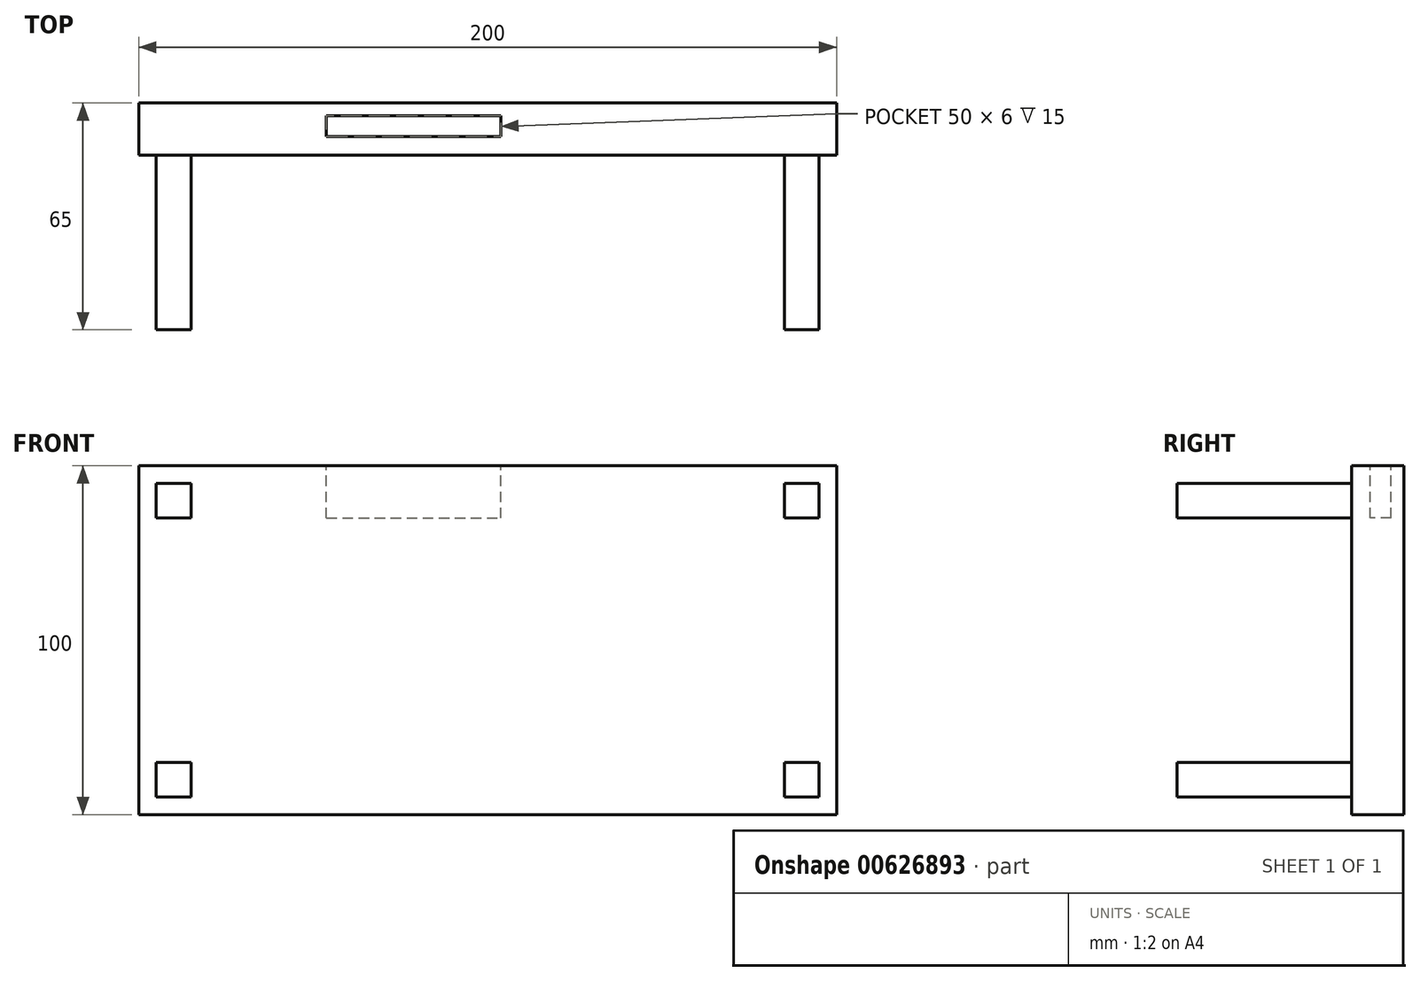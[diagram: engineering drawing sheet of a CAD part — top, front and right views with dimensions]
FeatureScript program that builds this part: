
annotation { "Feature Type Name" : "Feature", "Feature Type Description" : "" }
export const myFeature = defineFeature(function(context is Context, id is Id, definition is map)
    precondition{}
    {
        {
            var Q0;
            Q0=qCreatedBy(makeId("Front.planeOp"),FACE);
            var sketch = newSketch(context, id + "F0", { "sketchPlane" : qUnion([Q0])});
            skLineSegment(sketch, "E0.bottom", {"start": v(-53.8, 99.96) * mm, "end": v(146.2, 99.96) * mm});
            skLineSegment(sketch, "E0.top", {"start": v(-53.8, -0.04) * mm, "end": v(146.2, -0.04) * mm});
            skLineSegment(sketch, "E0.left", {"start": v(-53.8, 99.96) * mm, "end": v(-53.8, -0.04) * mm});
            skLineSegment(sketch, "E0.right", {"start": v(146.2, 99.96) * mm, "end": v(146.2, -0.04) * mm});
            skSolve(sketch);
        }
        {
            var Q0;
            Q0 = qSketchRegion(id + "F0", true);
            extrude(context, id + "F1", {"entities" : qUnion([Q0]), "depth" : 15 * mm, "offsetDistance" : 25 * mm});
        }
        {
            var Q0;
            Q0=makeQuery(id+"F1.opExtrude","CAP_FACE",FACE,{"disambiguationData":[OSD([sQuery(id+"F0.wireOp",EDGE,"E0.bottom"),sQuery(id+"F0.wireOp",EDGE,"E0.top"),sQuery(id+"F0.wireOp",EDGE,"E0.left"),sQuery(id+"F0.wireOp",EDGE,"E0.right")])],"isStart":false});
            var sketch = newSketch(context, id + "F2", { "sketchPlane" : qUnion([Q0])});
            skLineSegment(sketch, "E1.bottom", {"start": v(-48.8, 94.96) * mm, "end": v(-38.8, 94.96) * mm});
            skLineSegment(sketch, "E1.top", {"start": v(-48.8, 84.96) * mm, "end": v(-38.8, 84.96) * mm});
            skLineSegment(sketch, "E1.left", {"start": v(-48.8, 94.96) * mm, "end": v(-48.8, 84.96) * mm});
            skLineSegment(sketch, "E1.right", {"start": v(-38.8, 94.96) * mm, "end": v(-38.8, 84.96) * mm});
            skLineSegment(sketch, "E2.bottom", {"start": v(-48.8, 14.96) * mm, "end": v(-38.8, 14.96) * mm});
            skLineSegment(sketch, "E2.top", {"start": v(-48.8, 4.96) * mm, "end": v(-38.8, 4.96) * mm});
            skLineSegment(sketch, "E2.left", {"start": v(-48.8, 14.96) * mm, "end": v(-48.8, 4.96) * mm});
            skLineSegment(sketch, "E2.right", {"start": v(-38.8, 14.96) * mm, "end": v(-38.8, 4.96) * mm});
            skLineSegment(sketch, "E3.bottom", {"start": v(131.2, 94.96) * mm, "end": v(141.2, 94.96) * mm});
            skLineSegment(sketch, "E3.top", {"start": v(131.2, 84.96) * mm, "end": v(141.2, 84.96) * mm});
            skLineSegment(sketch, "E3.left", {"start": v(131.2, 94.96) * mm, "end": v(131.2, 84.96) * mm});
            skLineSegment(sketch, "E3.right", {"start": v(141.2, 94.96) * mm, "end": v(141.2, 84.96) * mm});
            skLineSegment(sketch, "E4.bottom", {"start": v(131.2, 14.96) * mm, "end": v(141.2, 14.96) * mm});
            skLineSegment(sketch, "E4.top", {"start": v(131.2, 4.96) * mm, "end": v(141.2, 4.96) * mm});
            skLineSegment(sketch, "E4.left", {"start": v(131.2, 14.96) * mm, "end": v(131.2, 4.96) * mm});
            skLineSegment(sketch, "E4.right", {"start": v(141.2, 14.96) * mm, "end": v(141.2, 4.96) * mm});
            skSolve(sketch);
        }
        {
            var Q0;
            Q0 = qSketchRegion(id + "F2", true);
            var Q1;
            Q1 = qSketchRegion(id + "F4", true);
            extrude(context, id + "F3", {"entities" : qUnion([Q0, Q1]), "operationType" : NewBodyOperationType.ADD, "depth" : 50 * mm, "offsetDistance" : 25 * mm});
        }
        {
            var Q0;
            Q0=makeQuery(id+"F3.opExtrude","SWEPT_FACE",FACE,{"disambiguationData":[OSD([sQuery(id+"F2.wireOp",EDGE,"E1.bottom")])]});
            var sketch = newSketch(context, id + "F4", { "sketchPlane" : qUnion([Q0])});
            skLineSegment(sketch, "E5.left", {"start": v(0, -3.65) * mm, "end": v(0, -9.65) * mm});
            skLineSegment(sketch, "E5.right", {"start": v(50, -3.65) * mm, "end": v(50, -9.65) * mm});
            skLineSegment(sketch, "E6", {"start": v(0, -9.65) * mm, "end": v(50, -9.65) * mm});
            skLineSegment(sketch, "E7", {"start": v(0, -3.65) * mm, "end": v(50, -3.65) * mm});
            skSolve(sketch);
        }
        {
            var Q0;
            Q0 = qSketchRegion(id + "F4", true);
            extrude(context, id + "F5", {"entities" : qUnion([Q0]), "operationType" : NewBodyOperationType.REMOVE, "endBound" : BoundingType.SYMMETRIC, "oppositeDirection" : true, "depth" : 20 * mm, "offsetDistance" : 25 * mm});
        }
    });
